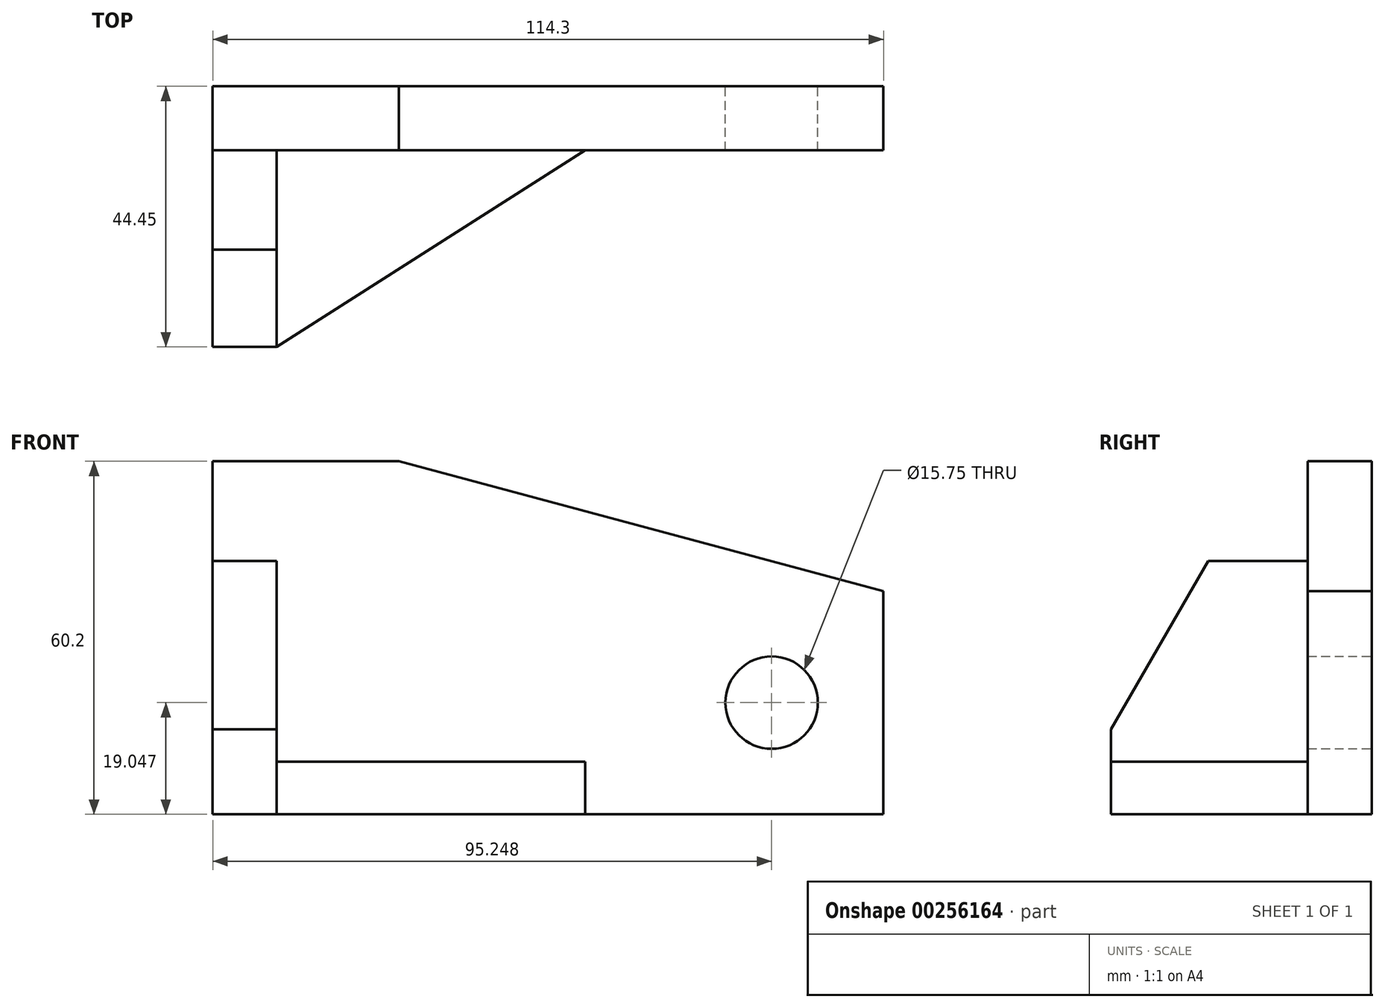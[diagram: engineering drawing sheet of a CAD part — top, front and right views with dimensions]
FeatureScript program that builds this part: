
annotation { "Feature Type Name" : "Feature", "Feature Type Description" : "" }
export const myFeature = defineFeature(function(context is Context, id is Id, definition is map)
    precondition{}
    {
        {
            var Q0;
            Q0=qCreatedBy(makeId("Front.planeOp"),FACE);
            var sketch = newSketch(context, id + "F0", { "sketchPlane" : qUnion([Q0])});
            skLineSegment(sketch, "E0", {"start": v(-49.86, 44.15) * mm, "end": v(-18.11, 44.15) * mm});
            skLineSegment(sketch, "E1", {"start": v(-18.11, 44.15) * mm, "end": v(64.44, 22.03) * mm});
            skLineSegment(sketch, "E2", {"start": v(-49.86, 44.15) * mm, "end": v(-49.86, -16.05) * mm});
            skLineSegment(sketch, "E3", {"start": v(64.44, 22.03) * mm, "end": v(64.44, -16.05) * mm});
            skLineSegment(sketch, "E4", {"start": v(-49.86, -16.05) * mm, "end": v(64.44, -16.05) * mm});
            skCircle(sketch, "E5", {"center": v(45.39, 3) * mm, "radius": 7.87 * mm});
            skLineSegment(sketch, "E6", {"start": v(-49.86, 27.18) * mm, "end": v(-38.94, 27.18) * mm});
            skLineSegment(sketch, "E7", {"start": v(-38.94, 27.18) * mm, "end": v(-38.94, -7.09) * mm});
            skLineSegment(sketch, "E8", {"start": v(-38.94, -7.09) * mm, "end": v(13.64, -7.09) * mm});
            skLineSegment(sketch, "E9", {"start": v(13.64, -16.05) * mm, "end": v(13.64, -7.09) * mm});
            skSolve(sketch);
        }
        {
            var Q0;
            Q0 = qSketchRegion(id + "F0", true);
            extrude(context, id + "F1", {"entities" : qUnion([Q0]), "depth" : 10.92 * mm});
        }
        {
            var Q0;
            {var subQ0=sQuery(id+"F0.wireOp",EDGE,"E6");Q0=makeQuery(id+"F0.imprint","IMPRINT",FACE,{"disambiguationData":[TD([[makeQuery(id+"F0.imprint","IMPRINT",EDGE,{"derivedFrom":subQ0}),-1.0]])]});}
            extrude(context, id + "F2", {"entities" : qUnion([Q0]), "operationType" : NewBodyOperationType.ADD, "depth" : 44.45 * mm});
        }
        {
            var Q0;
            Q0=makeQuery(id+"F2.opExtrude","SWEPT_FACE",FACE,{"disambiguationData":[OSD([sQuery(id+"F0.wireOp",EDGE,"E8")])]});
            var sketch = newSketch(context, id + "F3", { "sketchPlane" : qUnion([Q0])});
            skLineSegment(sketch, "E10", {"start": v(-38.94, -44.45) * mm, "end": v(13.64, -10.92) * mm});
            skSolve(sketch);
        }
        {
            var Q0;
            Q0=makeQuery(id+"F3.imprint","IMPRINT",FACE,{"disambiguationData":[TD([[makeQuery(id+"F3.imprint","IMPRINT",EDGE,{"derivedFrom":sQuery(id+"F3.wireOp",EDGE,"E10")}),-1.0]])]});
            extrude(context, id + "F4", {"entities" : qUnion([Q0]), "operationType" : NewBodyOperationType.REMOVE, "oppositeDirection" : true, "depth" : 10.92 * mm});
        }
        {
            var Q0;
            Q0=makeQuery(id+"F2.opExtrude","CAP_EDGE",EDGE,{"disambiguationData":[OSD([sQuery(id+"F0.wireOp",EDGE,"E6")])],"isStart":false});
            chamfer(context, id + "F5", {"entities" : qUnion([Q0]), "chamferType" : ChamferType.OFFSET_ANGLE, "width" : 28.7 * mm, "oppositeDirection" : true, "angle" : 30 * degree, "tangentPropagation" : true});
        }
    });
